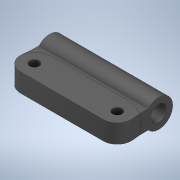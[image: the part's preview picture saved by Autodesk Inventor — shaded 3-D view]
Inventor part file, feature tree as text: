
AUTODESK INVENTOR PART (.ipt)
format: ipt  version: 2020 (Build 240168000, 168)  size: 324,096 bytes
history: native  units: in
note: dims shown in document units (in); Inventor stores cm internally (conversion verified against a paired STEP export)
features: extrude x9, sketch x9, projected_geometry x4
ambient origin geometry x8: Origin, YZ Plane, XZ Plane, XY Plane, X Axis, Y Axis, Z Axis, Center Point
bodies: Solid2 (feature_tree), Solid1 (feature_tree)
feature tree (22):
  extrude  "remove 6mm standoffs"  Depth=0.1181in
  extrude  "add 5mm left side"  Depth=0.3937in TaperAngle=0.0deg
  extrude  "add 5mm right side"  Depth=0.3937in TaperAngle=0.0deg
  extrude  "remove old chamfer"  Depth=0.3937in TaperAngle=0.0deg
  sketch  "Sketch5"  dims[d13=0.1181in d14=0.0in d15=0.1181in d16=0.0in]
  extrude  "Extrusion5"  Depth=0.1181in TaperAngle=0.0deg
  sketch  "Sketch7"
  extrude  "make standoff hole bigger"  Depth=0.2362in TaperAngle=0.0deg
  extrude  "new chamfer base"  [1 undecoded]
  extrude  "right side new chamfer"  [1 undecoded]
  extrude  "left side new chamfer"  [1 undecoded]
  sketch  "Sketch1"  dims[d0=0.1181in d1=0.1181in]
  sketch  "Sketch2"  dims[d2=0.3937in d3=0.0in d4=0.1969in d5=0.0in]
  sketch  "Sketch3"  dims[d6=0.1969in d7=0.0in d8=0.3937in d9=0.0in]
  sketch  "Sketch4"  dims[d10=0.2008in d11=0.3937in d12=0.0in]
  projected_geometry  "Projected Loop1"
  projected_geometry  "Projected Loop2"
  projected_geometry  "Projected Loop3"
  sketch  "Sketch6"  dims[d17=0.2362in d18=0.0in d19=0.2362in d20=0.0in]
  projected_geometry  "Projected Loop4"
  sketch  "Sketch9"
  sketch  "Sketch10"
note: 3 required parameter values undecoded (feature->parameter linkage not recoverable at this tier; creation-order binding heuristic only, values carry confidence <= 0.55)
